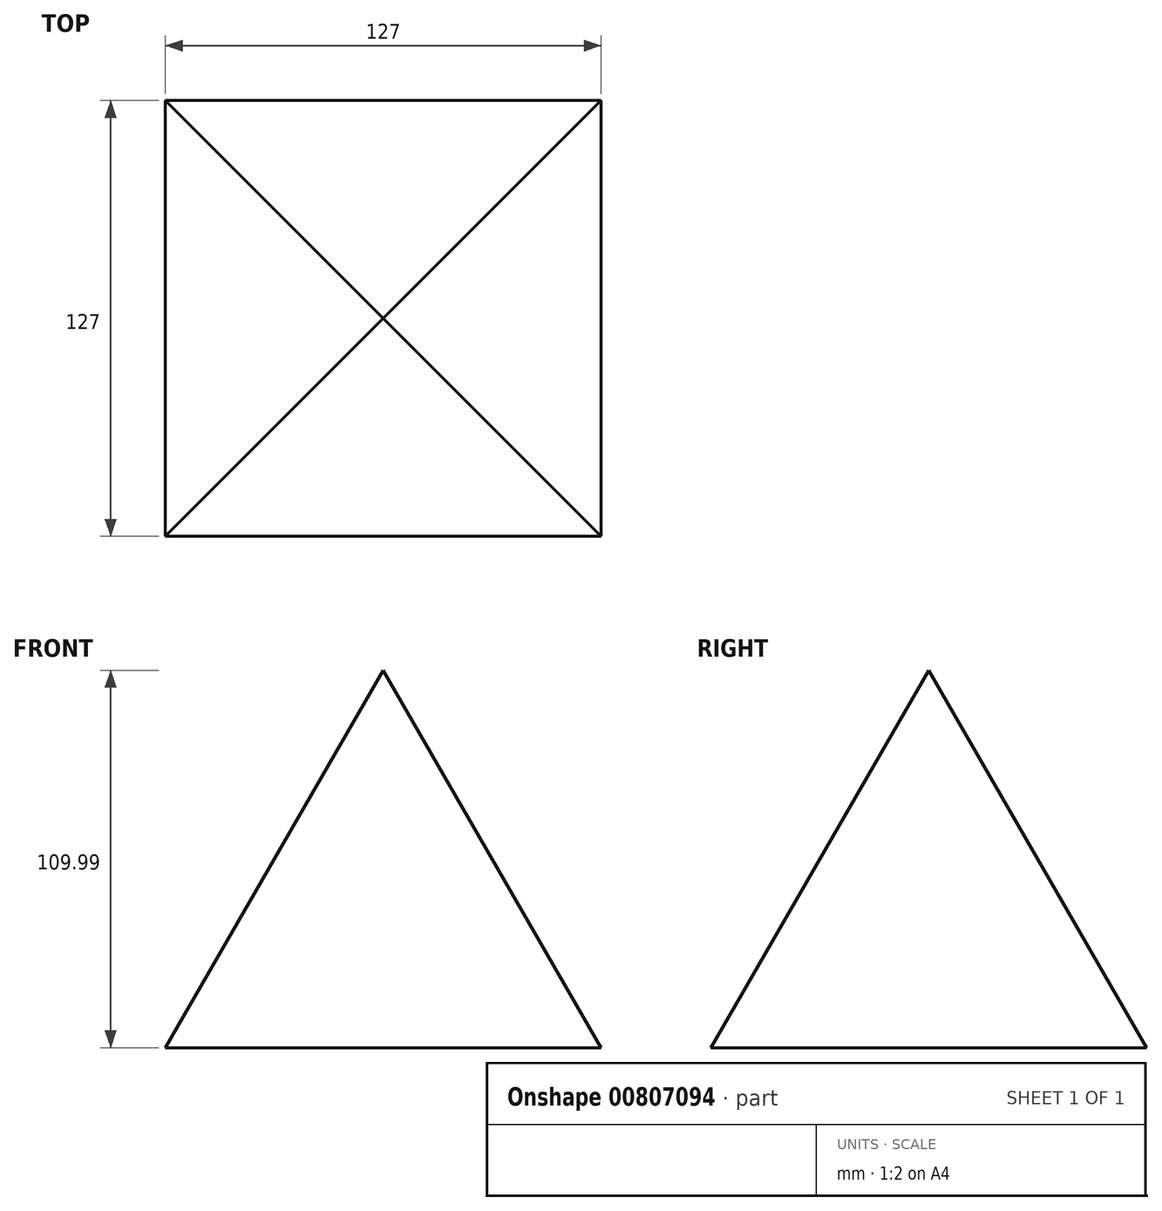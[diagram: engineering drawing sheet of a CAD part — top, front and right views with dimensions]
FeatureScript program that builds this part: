
annotation { "Feature Type Name" : "Feature", "Feature Type Description" : "" }
export const myFeature = defineFeature(function(context is Context, id is Id, definition is map)
    precondition{}
    {
        {
            var Q0;
            Q0=qCreatedBy(makeId("Top.planeOp"),FACE);
            var sketch = newSketch(context, id + "F0", { "sketchPlane" : qUnion([Q0])});
            skLineSegment(sketch, "E0.bottom", {"start": v(-63.27, 62.7) * mm, "end": v(63.73, 62.7) * mm});
            skLineSegment(sketch, "E0.top", {"start": v(-63.27, -64.3) * mm, "end": v(63.73, -64.3) * mm});
            skLineSegment(sketch, "E0.left", {"start": v(-63.27, 62.7) * mm, "end": v(-63.27, -64.3) * mm});
            skLineSegment(sketch, "E0.right", {"start": v(63.73, 62.7) * mm, "end": v(63.73, -64.3) * mm});
            skSolve(sketch);
        }
        {
            var Q0;
            Q0=makeQuery(id+"F0.imprint","IMPRINT",FACE,{"disambiguationData":[TD([[makeQuery(id+"F0.imprint","IMPRINT",EDGE,{"derivedFrom":sQuery(id+"F0.wireOp",EDGE,"E0.bottom")}),-1.0]])]});
            extrude(context, id + "F1", {"entities" : qUnion([Q0]), "depth" : 223.52 * mm, "offsetDistance" : 25.4 * mm, "hasDraft" : true, "draftAngle" : 30 * degree, "draftPullDirection" : true});
        }
    });
